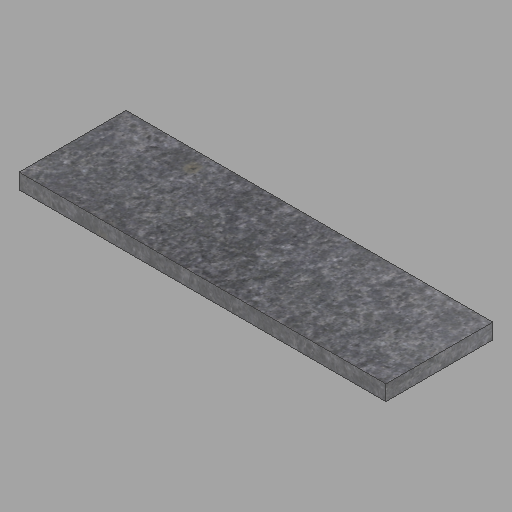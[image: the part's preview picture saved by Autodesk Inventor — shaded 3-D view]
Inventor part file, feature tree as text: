
AUTODESK INVENTOR PART (.ipt)
format: ipt  version: 2023 (Build 270158000, 158)  size: 203,264 bytes
history: native  units: in
note: dims shown in document units (in); Inventor stores cm internally (conversion verified against a paired STEP export)
features: other x1, extrude x1, sketch x1
ambient origin geometry x8: Origin, YZ Plane, XZ Plane, XY Plane, X Axis, Y Axis, Z Axis, Center Point
bodies: Solid1 (feature_tree)
feature tree (3):
  other  "2x14x48-8"
  extrude  "Extrusion1"  Depth=2.0in
  sketch  "Sketch1"  dims[d0=14.0in d1=2.0in d2=48.0in d3=0.0in]
